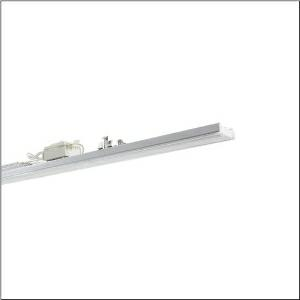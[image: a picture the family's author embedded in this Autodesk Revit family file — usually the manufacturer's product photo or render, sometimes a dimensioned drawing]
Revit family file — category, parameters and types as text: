
# Revit family: licross_21_recessed_mo_52te107n485g
name_source: partatom
category: Lighting Fixtures
units: mm (PartAtom-declared; Revit-internal decimal feet)

## family parameters
Cut with Voids When Loaded = No
Host = Face
Light Source = No
Part Type = Normal
Room Calculation Point = No
Round Connector Dimension = Use Diameter
Shared = No

## types (1)
- Licross 21 Recessed MO (1 x LED, 8580 lm, 47.9 W, 4000K)
    Apparent Load = 48 VA
    CIE Flux Codes = 50 81 96 100 100
    Color Rendering = 80
    Color Temperature = 4000K
    Default Elevation = 1800 mm
    Description = Licross 21 Recessed MO, luminaire insert, of sheet steel, galvanised, coil coated, white, length: 1.500mm, width: 66mm, height: 67mm, LED rated luminous flux: 8.560lm, light colour: 840, SDCM (Standard Deviation of Colour Matching)MacAdam ≤ 3 SDCM (initial), control gear: ON/OFF, with plug, 3-pole, with phase selection, mains connection: 220..240V, AC, 50/60Hz, rated input power: 48W, internal wiring halogen-free, primary optical cover: cover, of PMMA, light emission: direct distribution, primary light characteristic: symmetric, protection rating (complete): IP54, insulation class (complete): insulation class I (protective earthing), certification: CE, ENEC, VDE, UKCA, protection symbol: D if used in an environment with non-conductive dust loads with corresponding accessories, impact resistance: IK06, permissible ambient temperature for indoor applications: -35..+40°C, corresponds to IFS (International Featured Standards) requirements for safety and quality in the food industry, reducing of maximum allowable ambient temperature of 5°C with ceiling mounting, LABS conformity tested according to VDMA 24364:2018-05, The light source and the operating device comply with the requirements of the Ecodesign Regulation (EU) 2019/2020 and are replaceable in accordance with this regulation, packaging unit: 1 piece
    Height = 58 mm
    Lamp = 1 x LED
    Lamp Light Flux = 8580 lm
    Lamp Power = 47.9 W
    Lamp count = 1
    Length = 1500 mm
    Luminous efficacy = 179 lm/W
    Manufacturer = Siteco
    ModVariant = No
    Model = 52TE107N485G
    Mounting Place = Ceiling
    Mounting Type = Pendant
    Number of Poles = 1
    OnlyDefault = Yes
    Power Factor = 1
    Product Name = Licross 21 Recessed MO
    Product group = luminaire insert | ceiling pendant
    ProductGroupID = 901
    Protection Class = Protection class I
    Protection Degree = IP 54
    RLX_Detail_Level = 1
    RLX_Emergency_Light_Flux = 0 lm
    RLX_Emergency_Type = 0
    RLX_Emergency_Type_DB = No
    RlxData = <blob elided: 21033 chars, md5=20745c1b>
    Socket = socket
    Standby Power = 0 W
    System Light Flux = 8580 lm
    System Power = 48 W
    Type Comments = Product without accessories
    Type Image = l_1296930.jpg
    URL = http://relux.com
    VarID = ---
    Voltage = 0 V
    Weight = 0.00 kg
    Width = 66 mm

## geometry (parser evidence)
native form markers: Blend x4, Sweep x11
no freeform markers — native parametric forms only
